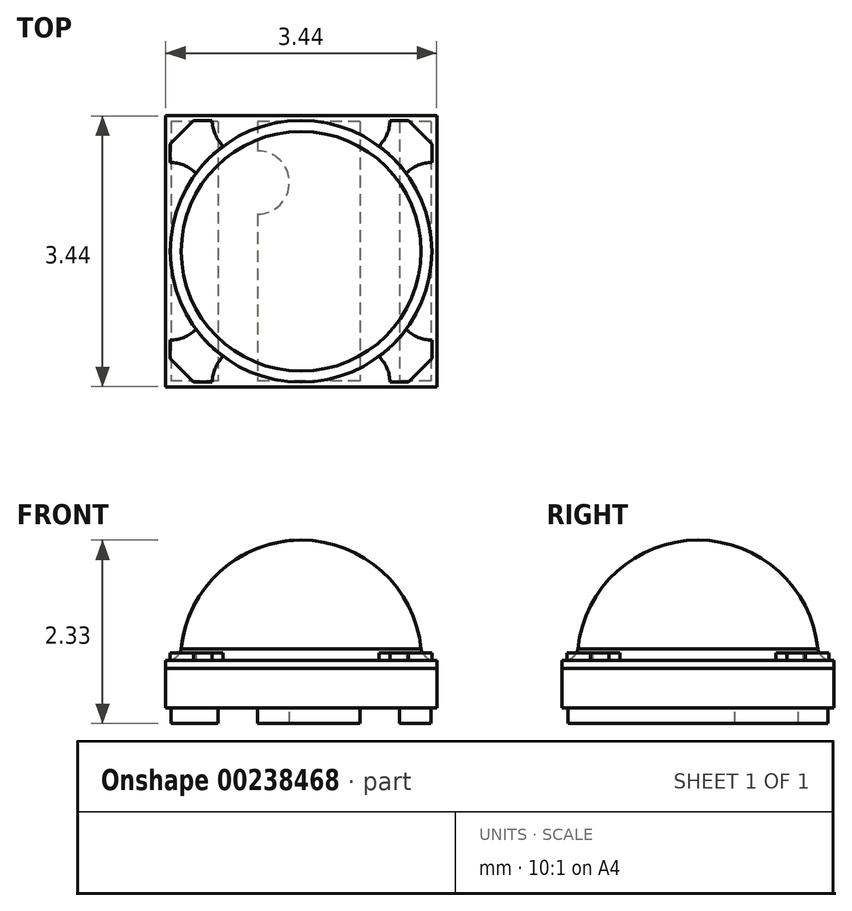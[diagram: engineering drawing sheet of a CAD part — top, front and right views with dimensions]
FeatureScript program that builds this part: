
annotation { "Feature Type Name" : "Feature", "Feature Type Description" : "" }
export const myFeature = defineFeature(function(context is Context, id is Id, definition is map)
    precondition{}
    {
        {
            var Q0;
            Q0=qCreatedBy(makeId("Top.planeOp"),FACE);
            var sketch = newSketch(context, id + "F0", { "sketchPlane" : qUnion([Q0])});
            skLineSegment(sketch, "E0.bottom", {"start": v(-1.72, 1.72) * mm, "end": v(1.73, 1.72) * mm});
            skLineSegment(sketch, "E0.top", {"start": v(-1.73, -1.73) * mm, "end": v(1.73, -1.73) * mm});
            skLineSegment(sketch, "E0.left", {"start": v(-1.72, 1.72) * mm, "end": v(-1.73, -1.73) * mm});
            skLineSegment(sketch, "E0.right", {"start": v(1.73, 1.72) * mm, "end": v(1.73, -1.73) * mm});
            skPoint(sketch, "E0.middle", {"position": v(0, 0) * mm});
            skSolve(sketch);
        }
        {
            var Q0;
            Q0 = qSketchRegion(id + "F0", true);
            extrude(context, id + "F1", {"entities" : qUnion([Q0]), "oppositeDirection" : true, "depth" : .5 * mm});
        }
        {
            var Q0;
            Q0=makeQuery(id+"F1.opExtrude","CAP_FACE",FACE,{"disambiguationData":[OSD([sQuery(id+"F0.wireOp",EDGE,"E0.bottom"),sQuery(id+"F0.wireOp",EDGE,"E0.top"),sQuery(id+"F0.wireOp",EDGE,"E0.left"),sQuery(id+"F0.wireOp",EDGE,"E0.right")])],"isStart":true});
            extrude(context, id + "F2", {"entities" : qUnion([Q0]), "depth" : .1 * mm});
        }
        {
            var Q0;
            Q0=qCreatedBy(makeId("Front.planeOp"),FACE);
            var sketch = newSketch(context, id + "F3", { "sketchPlane" : qUnion([Q0])});
            skLineSegment(sketch, "E1", {"start": v(0, 1.89) * mm, "end": v(0, -1.88) * mm, "construction": true});
            skArc(sketch, "E2", {"start": v(0, 1.63) * mm, "mid": v(-1.03, 1.23) * mm, "end": v(-1.52, 0.25) * mm});
            skArc(sketch, "E3", {"start": v(-1.66, 0.1) * mm, "mid": v(-1.57, 0.16) * mm, "end": v(-1.52, 0.25) * mm});
            skLineSegment(sketch, "E4", {"start": v(-1.66, 0.1) * mm, "end": v(0, 0.1) * mm});
            skLineSegment(sketch, "E5", {"start": v(0, 1.63) * mm, "end": v(0, 0.1) * mm});
            skSolve(sketch);
        }
        {
            var Q0;
            Q0 = qSketchRegion(id + "F3", true);
            var Q1;
            Q1=sQuery(id+"F3.wireOp",EDGE,"E1");
            revolve(context, id + "F4", {"entities" : qUnion([Q0]), "axis" : qUnion([Q1]), "revolveType" : RevolveType.FULL});
        }
        {
            var Q0;
            Q0=makeQuery(id+"F2.opExtrude","CAP_FACE",FACE,{"disambiguationData":[OSD([sQuery(id+"F0.wireOp",EDGE,"E0.bottom"),sQuery(id+"F0.wireOp",EDGE,"E0.top"),sQuery(id+"F0.wireOp",EDGE,"E0.left"),sQuery(id+"F0.wireOp",EDGE,"E0.right")])],"isStart":false});
            var sketch = newSketch(context, id + "F5", { "sketchPlane" : qUnion([Q0])});
            skLineSegment(sketch, "E6", {"start": v(-1.73, -1.73) * mm, "end": v(1.73, 1.72) * mm, "construction": true});
            skLineSegment(sketch, "E7", {"start": v(-1.66, -1.36) * mm, "end": v(-1.51, -1.51) * mm});
            skLineSegment(sketch, "E8", {"start": v(-1.34, -0.99) * mm, "end": v(-1.34, -1) * mm});
            skArc(sketch, "E9.filletArc", {"start": v(-1.66, -1.13) * mm, "mid": v(-1.49, -1.1) * mm, "end": v(-1.34, -1) * mm});
            skArc(sketch, "E10", {"start": v(-1.18, -1.18) * mm, "mid": v(-1.26, -1.09) * mm, "end": v(-1.34, -0.99) * mm});
            skLineSegment(sketch, "E11.trimOffspring", {"start": v(-1.66, -1.36) * mm, "end": v(-1.66, -1.13) * mm});
            skLineSegment(sketch, "E12.MirrorCS", {"start": v(-1.36, -1.66) * mm, "end": v(-1.51, -1.51) * mm});
            skLineSegment(sketch, "E13.MirrorCS", {"start": v(-1.36, -1.66) * mm, "end": v(-1.13, -1.66) * mm});
            skArc(sketch, "E14.MirrorCS", {"start": v(-1.13, -1.66) * mm, "mid": v(-1.1, -1.49) * mm, "end": v(-1, -1.34) * mm});
            skLineSegment(sketch, "E15.MirrorCS", {"start": v(-0.99, -1.34) * mm, "end": v(-1, -1.34) * mm});
            skArc(sketch, "E16.MirrorCS", {"start": v(-1.18, -1.18) * mm, "mid": v(-1.09, -1.26) * mm, "end": v(-0.99, -1.34) * mm});
            skLineSegment(sketch, "E17", {"start": v(-1.72, 1.72) * mm, "end": v(1.73, -1.73) * mm, "construction": true});
            skLineSegment(sketch, "E18.MirrorCS", {"start": v(1.34, 0.99) * mm, "end": v(1.34, 1) * mm});
            skLineSegment(sketch, "E19.MirrorCS", {"start": v(0.99, 1.34) * mm, "end": v(1, 1.34) * mm});
            skArc(sketch, "E20.MirrorCS", {"start": v(1.18, 1.18) * mm, "mid": v(1.26, 1.09) * mm, "end": v(1.34, 0.99) * mm});
            skLineSegment(sketch, "E21.MirrorCS", {"start": v(1.66, 1.36) * mm, "end": v(1.51, 1.51) * mm});
            skLineSegment(sketch, "E22.MirrorCS", {"start": v(1.36, 1.66) * mm, "end": v(1.13, 1.66) * mm});
            skLineSegment(sketch, "E23.MirrorCS", {"start": v(1.66, 1.36) * mm, "end": v(1.66, 1.13) * mm});
            skArc(sketch, "E24.MirrorCS", {"start": v(1.18, 1.18) * mm, "mid": v(1.09, 1.26) * mm, "end": v(0.99, 1.34) * mm});
            skArc(sketch, "E25.MirrorCS", {"start": v(1.13, 1.66) * mm, "mid": v(1.1, 1.49) * mm, "end": v(1, 1.34) * mm});
            skLineSegment(sketch, "E26.MirrorCS", {"start": v(1.36, 1.66) * mm, "end": v(1.51, 1.51) * mm});
            skArc(sketch, "E27.MirrorCS", {"start": v(1.66, 1.13) * mm, "mid": v(1.49, 1.1) * mm, "end": v(1.34, 1) * mm});
            skLineSegment(sketch, "E28", {"start": v(0, 0) * mm, "end": v(1.73, 0) * mm, "construction": true});
            skLineSegment(sketch, "E29.MirrorCS", {"start": v(-0.99, 1.34) * mm, "end": v(-1, 1.34) * mm});
            skLineSegment(sketch, "E30.MirrorCS", {"start": v(-1.34, 0.99) * mm, "end": v(-1.34, 1) * mm});
            skArc(sketch, "E31.MirrorCS", {"start": v(-1.13, 1.66) * mm, "mid": v(-1.1, 1.49) * mm, "end": v(-1, 1.34) * mm});
            skLineSegment(sketch, "E32.MirrorCS", {"start": v(-1.36, 1.66) * mm, "end": v(-1.13, 1.66) * mm});
            skLineSegment(sketch, "E33.MirrorCS", {"start": v(-1.36, 1.66) * mm, "end": v(-1.51, 1.51) * mm});
            skLineSegment(sketch, "E34.MirrorCS", {"start": v(-1.66, 1.36) * mm, "end": v(-1.66, 1.13) * mm});
            skArc(sketch, "E35.MirrorCS", {"start": v(-1.18, 1.18) * mm, "mid": v(-1.26, 1.09) * mm, "end": v(-1.34, 0.99) * mm});
            skArc(sketch, "E36.MirrorCS", {"start": v(-1.66, 1.13) * mm, "mid": v(-1.49, 1.1) * mm, "end": v(-1.34, 1) * mm});
            skArc(sketch, "E37.MirrorCS", {"start": v(-1.18, 1.18) * mm, "mid": v(-1.09, 1.26) * mm, "end": v(-0.99, 1.34) * mm});
            skLineSegment(sketch, "E38.MirrorCS", {"start": v(-1.66, 1.36) * mm, "end": v(-1.51, 1.51) * mm});
            skLineSegment(sketch, "E39.MirrorCS", {"start": v(1.34, -0.99) * mm, "end": v(1.34, -1) * mm});
            skLineSegment(sketch, "E40.MirrorCS", {"start": v(0.99, -1.34) * mm, "end": v(1, -1.34) * mm});
            skLineSegment(sketch, "E41.MirrorCS", {"start": v(1.66, -1.36) * mm, "end": v(1.66, -1.13) * mm});
            skArc(sketch, "E42.MirrorCS", {"start": v(1.66, -1.13) * mm, "mid": v(1.49, -1.1) * mm, "end": v(1.34, -1) * mm});
            skLineSegment(sketch, "E43.MirrorCS", {"start": v(1.66, -1.36) * mm, "end": v(1.51, -1.51) * mm});
            skLineSegment(sketch, "E44.MirrorCS", {"start": v(1.36, -1.66) * mm, "end": v(1.13, -1.66) * mm});
            skLineSegment(sketch, "E45.MirrorCS", {"start": v(1.36, -1.66) * mm, "end": v(1.51, -1.51) * mm});
            skArc(sketch, "E46.MirrorCS", {"start": v(1.13, -1.66) * mm, "mid": v(1.1, -1.49) * mm, "end": v(1, -1.34) * mm});
            skArc(sketch, "E47.MirrorCS", {"start": v(1.18, -1.18) * mm, "mid": v(1.09, -1.26) * mm, "end": v(0.99, -1.34) * mm});
            skArc(sketch, "E48.MirrorCS", {"start": v(1.18, -1.18) * mm, "mid": v(1.26, -1.09) * mm, "end": v(1.34, -0.99) * mm});
            skSolve(sketch);
        }
        {
            var Q0;
            Q0 = qSketchRegion(id + "F5", true);
            extrude(context, id + "F6", {"entities" : qUnion([Q0]), "depth" : .1 * mm});
        }
        {
            var Q0;
            Q0=makeQuery(id+"F1.opExtrude","CAP_FACE",FACE,{"disambiguationData":[OSD([sQuery(id+"F0.wireOp",EDGE,"E0.bottom"),sQuery(id+"F0.wireOp",EDGE,"E0.top"),sQuery(id+"F0.wireOp",EDGE,"E0.left"),sQuery(id+"F0.wireOp",EDGE,"E0.right")])],"isStart":false});
            var sketch = newSketch(context, id + "F7", { "sketchPlane" : qUnion([Q0])});
            skLineSegment(sketch, "E49.bottom", {"start": v(1.65, -1.65) * mm, "end": v(1.25, -1.65) * mm});
            skLineSegment(sketch, "E49.top", {"start": v(1.65, 1.65) * mm, "end": v(1.25, 1.65) * mm});
            skLineSegment(sketch, "E49.left", {"start": v(1.65, -1.65) * mm, "end": v(1.65, 1.65) * mm});
            skLineSegment(sketch, "E49.right", {"start": v(-1.65, -1.65) * mm, "end": v(-1.65, 1.65) * mm});
            skPoint(sketch, "E49.middle", {"position": v(0, 0) * mm});
            skLineSegment(sketch, "E50", {"start": v(1.25, -1.65) * mm, "end": v(1.25, 1.65) * mm});
            skLineSegment(sketch, "E51", {"start": v(-1.05, -1.65) * mm, "end": v(-1.05, 1.65) * mm});
            skLineSegment(sketch, "E52", {"start": v(0.75, -1.65) * mm, "end": v(0.75, 1.65) * mm});
            skLineSegment(sketch, "E53", {"start": v(-0.55, -1.65) * mm, "end": v(-0.55, -1.28) * mm});
            skArc(sketch, "E54", {"start": v(-0.55, -1.28) * mm, "mid": v(-0.15, -0.87) * mm, "end": v(-0.55, -0.47) * mm});
            skLineSegment(sketch, "E55.trimOffspring", {"start": v(-0.55, -0.47) * mm, "end": v(-0.55, 1.65) * mm});
            skLineSegment(sketch, "E56.trimOffspring", {"start": v(-1.05, -1.65) * mm, "end": v(-1.65, -1.65) * mm});
            skLineSegment(sketch, "E57.trimOffspring", {"start": v(-1.05, 1.65) * mm, "end": v(-1.65, 1.65) * mm});
            skLineSegment(sketch, "E58.trimOffspring", {"start": v(0.75, 1.65) * mm, "end": v(-0.55, 1.65) * mm});
            skLineSegment(sketch, "E59.trimOffspring", {"start": v(0.75, -1.65) * mm, "end": v(-0.55, -1.65) * mm});
            skSolve(sketch);
        }
        {
            var Q0;
            Q0 = qSketchRegion(id + "F7", true);
            extrude(context, id + "F8", {"entities" : qUnion([Q0]), "depth" : .2 * mm});
        }
    });
